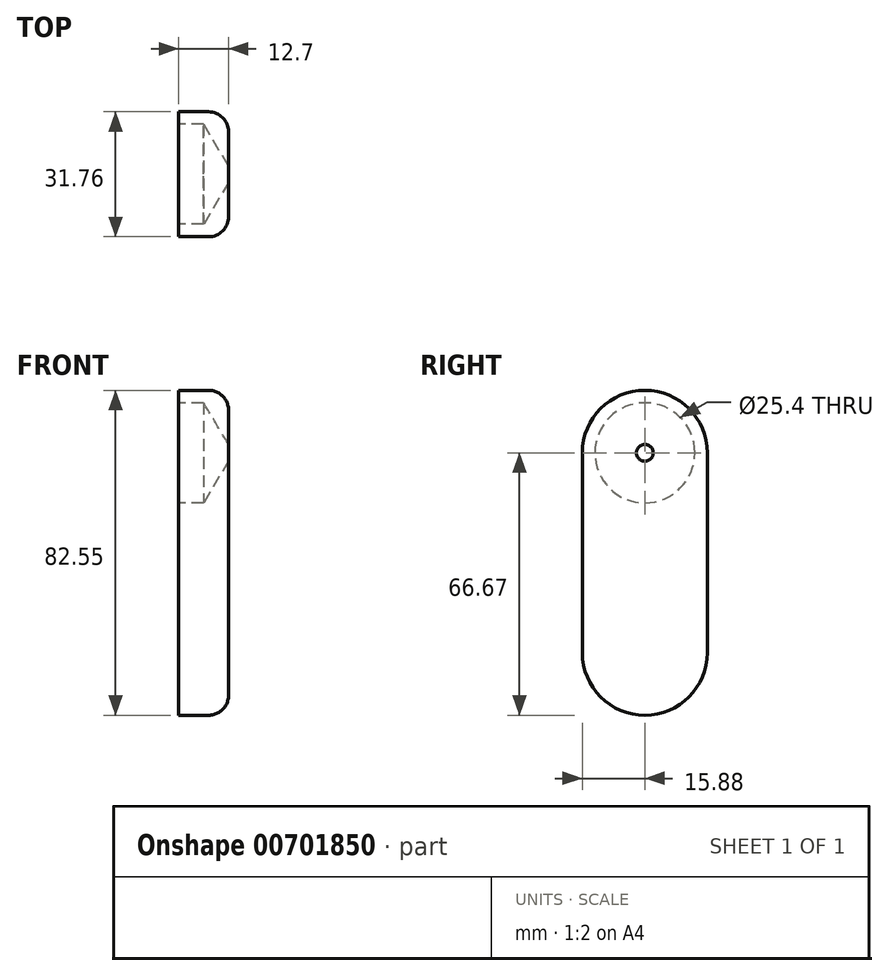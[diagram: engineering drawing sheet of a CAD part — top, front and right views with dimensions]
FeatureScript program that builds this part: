
annotation { "Feature Type Name" : "Feature", "Feature Type Description" : "" }
export const myFeature = defineFeature(function(context is Context, id is Id, definition is map)
    precondition{}
    {
        {
            var Q0;
            Q0=qCreatedBy(makeId("Right.planeOp"),FACE);
            var sketch = newSketch(context, id + "F0", { "sketchPlane" : qUnion([Q0])});
            skCircle(sketch, "E0", {"center": v(0, 0) * mm, "radius": 15.88 * mm});
            skCircle(sketch, "E1", {"center": v(0, -50.8) * mm, "radius": 15.88 * mm});
            skLineSegment(sketch, "E2", {"start": v(15.88, 0) * mm, "end": v(15.88, -50.8) * mm});
            skLineSegment(sketch, "E3", {"start": v(-15.88, 0) * mm, "end": v(-15.88, -50.8) * mm});
            skSolve(sketch);
        }
        {
            var Q0;
            Q0 = qSketchRegion(id + "F0", true);
            var Q1;
            Q1 = qSketchRegion(id + "FpAsST0IxCC8lKH_1", true);
            extrude(context, id + "F1", {"entities" : qUnion([Q0, Q1]), "depth" : 12.7 * mm, "offsetDistance" : 25.4 * mm});
        }
        {
            var Q0;
            Q0=makeQuery(id+"F1.opExtrude","CAP_FACE",FACE,{"disambiguationData":[OSD([sQuery(id+"F0.wireOp",EDGE,"E0"),sQuery(id+"F0.wireOp",EDGE,"E1"),sQuery(id+"F0.wireOp",EDGE,"E2"),sQuery(id+"F0.wireOp",EDGE,"E3")])],"isStart":false});
            fillet(context, id + "F2", {"entities" : qUnion([Q0]), "radius" : 5.08 * mm, "tangentPropagation" : true, "allowEdgeOverflow" : false});
        }
        {
            var Q0;
            Q0=makeQuery(id+"F1.opExtrude","CAP_FACE",FACE,{"disambiguationData":[OSD([sQuery(id+"F0.wireOp",EDGE,"E0"),sQuery(id+"F0.wireOp",EDGE,"E1"),sQuery(id+"F0.wireOp",EDGE,"E2"),sQuery(id+"F0.wireOp",EDGE,"E3")])],"isStart":true});
            var sketch = newSketch(context, id + "F3", { "sketchPlane" : qUnion([Q0])});
            skCircle(sketch, "E4", {"center": v(0, 0) * mm, "radius": 12.7 * mm});
            skSolve(sketch);
        }
        {
            var Q0;
            Q0=sQuery(id+"F3.wireOp",VERTEX,"E4.center");
            var Q1;
            Q1=makeQuery(id+"F1.opExtrude","SWEPT_BODY",BODY,{"disambiguationData":[OSD([sQuery(id+"F0.wireOp",EDGE,"E0"),sQuery(id+"F0.wireOp",EDGE,"E1"),sQuery(id+"F0.wireOp",EDGE,"E2"),sQuery(id+"F0.wireOp",EDGE,"E3")])]});
            hole(context, id + "F4", {"style" : HoleStyle.SIMPLE, "endStyle" : HoleEndStyle.BLIND, "holeDiameter" : 25.4 * mm, "majorDiameter" : 6.35 * mm, "holeDepth" : 6.35 * mm, "isTappedThrough" : true, "tappedDepth" : 12.7 * mm, "tapClearance" : 3, "locations" : qUnion([Q0]), "scope" : qUnion([Q1])});
        }
    });
